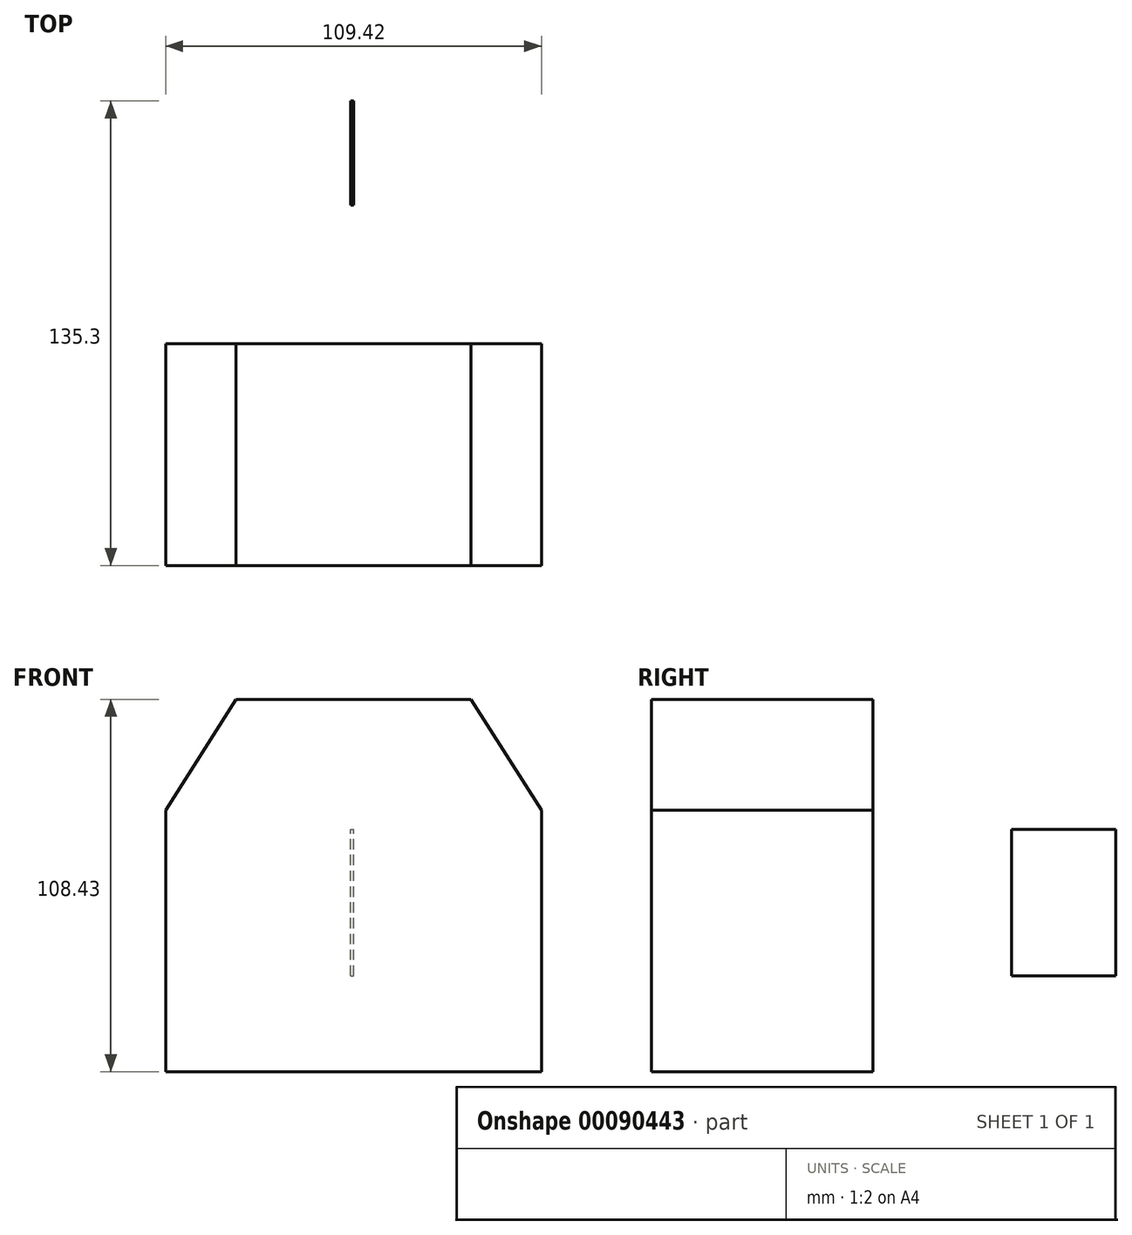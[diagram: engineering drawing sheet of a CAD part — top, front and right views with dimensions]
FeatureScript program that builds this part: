
annotation { "Feature Type Name" : "Feature", "Feature Type Description" : "" }
export const myFeature = defineFeature(function(context is Context, id is Id, definition is map)
    precondition{}
    {
        {
            var Q0;
            Q0=qCreatedBy(makeId("Front.planeOp"),FACE);
            var sketch = newSketch(context, id + "F0", { "sketchPlane" : qUnion([Q0])});
            skLineSegment(sketch, "E0.bottom", {"start": v(-54.71, 38.1) * mm, "end": v(54.71, 38.1) * mm});
            skLineSegment(sketch, "E0.top", {"start": v(-54.71, -38.1) * mm, "end": v(54.71, -38.1) * mm});
            skLineSegment(sketch, "E0.left", {"start": v(-54.71, 38.1) * mm, "end": v(-54.71, -38.1) * mm});
            skLineSegment(sketch, "E0.right", {"start": v(54.71, 38.1) * mm, "end": v(54.71, -38.1) * mm});
            skPoint(sketch, "E0.middle", {"position": v(0, 0) * mm});
            skLineSegment(sketch, "E1", {"start": v(-54.71, 38.1) * mm, "end": v(-34.23, 70.33) * mm});
            skLineSegment(sketch, "E2", {"start": v(-34.23, 70.33) * mm, "end": v(34.23, 70.33) * mm});
            skLineSegment(sketch, "E3", {"start": v(34.23, 70.33) * mm, "end": v(54.71, 38.1) * mm});
            skSolve(sketch);
        }
        {
            var Q0;
            Q0=makeQuery(id+"F0.imprint","IMPRINT",FACE,{"disambiguationData":[TD([[makeQuery(id+"F0.imprint","IMPRINT",EDGE,{"derivedFrom":sQuery(id+"F0.wireOp",EDGE,"E0.bottom")}),1.0]])]});
            var Q1;
            Q1=makeQuery(id+"F0.imprint","IMPRINT",FACE,{"disambiguationData":[TD([[makeQuery(id+"F0.imprint","IMPRINT",EDGE,{"derivedFrom":sQuery(id+"F0.wireOp",EDGE,"E0.bottom")}),-1.0]])]});
            extrude(context, id + "F1", {"entities" : qUnion([Q0, Q1]), "depth" : 39.2 * mm});
        }
        {
            var Q0;
            Q0=qCreatedBy(makeId("Top.planeOp"),FACE);
            var sketch = newSketch(context, id + "F2", { "sketchPlane" : qUnion([Q0])});
            skSolve(sketch);
        }
        {
            var Q0;
            Q0 = qSketchRegion(id + "F2", true);
            var Q1;
            Q1=makeQuery(id+"F1.opExtrude","CAP_FACE",FACE,{"disambiguationData":[OSD([sQuery(id+"F0.wireOp",EDGE,"E0.top"),sQuery(id+"F0.wireOp",EDGE,"E0.left"),sQuery(id+"F0.wireOp",EDGE,"E0.right"),sQuery(id+"F0.wireOp",EDGE,"E1"),sQuery(id+"F0.wireOp",EDGE,"E2"),sQuery(id+"F0.wireOp",EDGE,"E3")])],"isStart":true});
            extrude(context, id + "F3", {"entities" : qUnion([Q0, Q1]), "operationType" : NewBodyOperationType.ADD, "depth" : 25.4 * mm});
        }
        {
            var Q0;
            Q0=qCreatedBy(makeId("Right.planeOp"),FACE);
            var sketch = newSketch(context, id + "F4", { "sketchPlane" : qUnion([Q0])});
            skLineSegment(sketch, "E4.bottom", {"start": v(65.78, -10.16) * mm, "end": v(96.1, -10.16) * mm});
            skLineSegment(sketch, "E4.top", {"start": v(65.78, 32.41) * mm, "end": v(96.1, 32.41) * mm});
            skLineSegment(sketch, "E4.left", {"start": v(65.78, -10.16) * mm, "end": v(65.78, 32.41) * mm});
            skLineSegment(sketch, "E4.right", {"start": v(96.1, -10.16) * mm, "end": v(96.1, 32.41) * mm});
            skSolve(sketch);
        }
        {
            var Q0;
            Q0=makeQuery(id+"F4.imprint","IMPRINT",FACE,{"disambiguationData":[TD([[makeQuery(id+"F4.imprint","IMPRINT",EDGE,{"derivedFrom":sQuery(id+"F4.wireOp",EDGE,"E4.bottom")}),1.0]])]});
            extrude(context, id + "F5", {"entities" : qUnion([Q0]), "oppositeDirection" : true, "depth" : 0.89 * mm});
        }
    });
